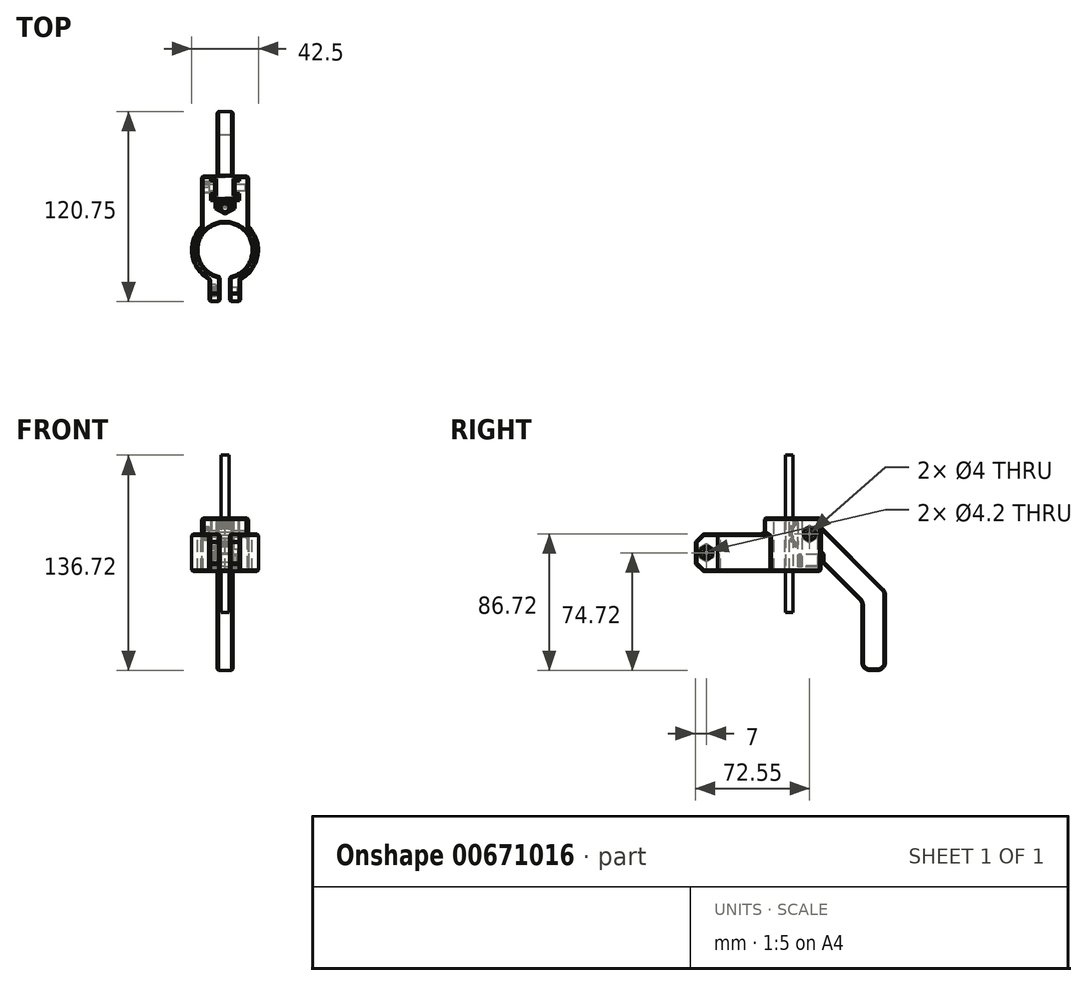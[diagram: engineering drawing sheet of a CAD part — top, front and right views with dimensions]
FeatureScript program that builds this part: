
annotation { "Feature Type Name" : "Feature", "Feature Type Description" : "" }
export const myFeature = defineFeature(function(context is Context, id is Id, definition is map)
    precondition{}
    {
        {
            var Q0;
            Q0=qCreatedBy(makeId("Top.planeOp"),FACE);
            var sketch = newSketch(context, id + "F0", { "sketchPlane" : qUnion([Q0])});
            skArc(sketch, "E0", {"start": v(3, -16.99) * mm, "mid": v(0, 17.25) * mm, "end": v(-3, -16.99) * mm});
            skLineSegment(sketch, "E1.top", {"start": v(3, -32.75) * mm, "end": v(10, -32.75) * mm});
            skLineSegment(sketch, "E1.left", {"start": v(3, -16.99) * mm, "end": v(3, -32.75) * mm});
            skLineSegment(sketch, "E1.right", {"start": v(10, -18.75) * mm, "end": v(10, -32.75) * mm});
            skLineSegment(sketch, "E2.MirrorCS", {"start": v(-10, -18.75) * mm, "end": v(-10, -32.75) * mm});
            skLineSegment(sketch, "E3.MirrorCS", {"start": v(-3, -32.75) * mm, "end": v(-10, -32.75) * mm});
            skLineSegment(sketch, "E4.MirrorCS", {"start": v(-3, -16.99) * mm, "end": v(-3, -32.75) * mm});
            skArc(sketch, "E5.trimOffspring", {"start": v(10, -18.75) * mm, "mid": v(21.02, -3.1) * mm, "end": v(15, 15.05) * mm});
            skArc(sketch, "E6.trimOffspring", {"start": v(-15, 15.05) * mm, "mid": v(-21.02, -3.1) * mm, "end": v(-10, -18.75) * mm});
            skLineSegment(sketch, "E7.top", {"start": v(-15, 47) * mm, "end": v(-5.25, 47) * mm});
            skLineSegment(sketch, "E7.left", {"start": v(-15, 8.52) * mm, "end": v(-15, 47) * mm});
            skLineSegment(sketch, "E7.right", {"start": v(15, 8.52) * mm, "end": v(15, 47) * mm});
            skLineSegment(sketch, "E8", {"start": v(0, 24) * mm, "end": v(-5.25, 27.03) * mm});
            skLineSegment(sketch, "E9", {"start": v(-5.25, 27.03) * mm, "end": v(-5.25, 47) * mm});
            skLineSegment(sketch, "E10", {"start": v(5.25, 47) * mm, "end": v(5.25, 27.03) * mm});
            skLineSegment(sketch, "E11", {"start": v(5.25, 27.03) * mm, "end": v(0, 24) * mm});
            skLineSegment(sketch, "E12.trimOffspring", {"start": v(5.25, 47) * mm, "end": v(15, 47) * mm});
            skSolve(sketch);
        }
        {
            var Q0;
            Q0=qSketchRegion(id+"F0",true);
            extrude(context, id + "F1", {"entities" : qUnion([Q0]), "oppositeDirection" : true, "depth" : 24 * mm, "offsetDistance" : 25 * mm});
        }
        {
            var Q0;
            Q0=makeQuery(id+"F1.opExtrude","SWEPT_FACE",FACE,{"disambiguationData":[OSD([sQuery(id+"F0.wireOp",EDGE,"E2.MirrorCS")])]});
            var sketch = newSketch(context, id + "F2", { "sketchPlane" : qUnion([Q0])});
            skLineSegment(sketch, "E13", {"start": v(25.75, 0) * mm, "end": v(25.75, -24) * mm, "construction": true});
            skCircle(sketch, "E14", {"center": v(25.75, -12) * mm, "radius": 2.1 * mm});
            skCircle(sketch, "E15.cCircle", {"center": v(25.75, -12) * mm, "radius": 3.7 * mm, "construction": true});
            skLineSegment(sketch, "E15.0", {"start": v(25.75, -7.73) * mm, "end": v(29.45, -9.86) * mm});
            skLineSegment(sketch, "E15.1", {"start": v(29.45, -9.86) * mm, "end": v(29.45, -11.5) * mm});
            skLineSegment(sketch, "E15.2", {"start": v(29.45, -14.14) * mm, "end": v(25.75, -16.27) * mm});
            skLineSegment(sketch, "E15.4", {"start": v(22.05, -14.14) * mm, "end": v(22.05, -9.86) * mm});
            skPoint(sketch, "E15.0.midPoint", {"position": v(27.6, -8.8) * mm});
            skLineSegment(sketch, "E16", {"start": v(29.45, -12.5) * mm, "end": v(28.95, -12) * mm});
            skLineSegment(sketch, "E17", {"start": v(28.95, -12) * mm, "end": v(29.45, -11.5) * mm});
            skLineSegment(sketch, "E18.trimOffspring", {"start": v(29.45, -12.5) * mm, "end": v(29.45, -14.14) * mm});
            skLineSegment(sketch, "E19.1.0", {"start": v(24.33, -8.55) * mm, "end": v(25.75, -7.73) * mm});
            skLineSegment(sketch, "E19.1.1", {"start": v(24.33, -8.55) * mm, "end": v(24.15, -9.23) * mm});
            skLineSegment(sketch, "E19.1.2", {"start": v(24.15, -9.23) * mm, "end": v(23.47, -9.05) * mm});
            skLineSegment(sketch, "E19.1.3", {"start": v(22.05, -9.86) * mm, "end": v(23.47, -9.05) * mm});
            skLineSegment(sketch, "E19.2.0", {"start": v(23.47, -14.95) * mm, "end": v(22.05, -14.14) * mm});
            skLineSegment(sketch, "E19.2.1", {"start": v(23.47, -14.95) * mm, "end": v(24.15, -14.77) * mm});
            skLineSegment(sketch, "E19.2.2", {"start": v(24.15, -14.77) * mm, "end": v(24.33, -15.45) * mm});
            skLineSegment(sketch, "E19.2.3", {"start": v(25.75, -16.27) * mm, "end": v(24.33, -15.45) * mm});
            skSolve(sketch);
        }
        {
            var Q0;
            Q0=makeQuery(id+"F2.imprint","IMPRINT",FACE,{"disambiguationData":[TD([[makeQuery(id+"F2.imprint","IMPRINT",EDGE,{"derivedFrom":sQuery(id+"F2.wireOp",EDGE,"E14")}),1.0]])]});
            extrude(context, id + "F3", {"entities" : qUnion([Q0]), "operationType" : NewBodyOperationType.REMOVE, "endBound" : BoundingType.THROUGH_ALL, "oppositeDirection" : true, "depth" : 25 * mm, "offsetDistance" : 25 * mm});
        }
        {
            var Q0;
            Q0=makeQuery(id+"F2.imprint","IMPRINT",FACE,{"disambiguationData":[TD([[makeQuery(id+"F2.imprint","IMPRINT",EDGE,{"derivedFrom":sQuery(id+"F2.wireOp",EDGE,"E14")}),-1.0]])]});
            extrude(context, id + "F4", {"entities" : qUnion([Q0]), "operationType" : NewBodyOperationType.REMOVE, "oppositeDirection" : true, "depth" : 4 * mm, "offsetDistance" : 25 * mm});
        }
        {
            var Q0;
            Q0=qCreatedBy(makeId("Top.planeOp"),FACE);
            var sketch = newSketch(context, id + "F5", { "sketchPlane" : qUnion([Q0])});
            skCircle(sketch, "E20", {"center": v(0, 26.89) * mm, "radius": 2.5 * mm});
            skSolve(sketch);
        }
        {
            var Q0;
            Q0 = qSketchRegion(id + "F5", true);
            extrude(context, id + "F6", {"entities" : qUnion([Q0]), "operationType" : NewBodyOperationType.ADD, "endBound" : BoundingType.SYMMETRIC, "depth" : 100 * mm, "offsetDistance" : 25 * mm});
        }
        {
            var Q0;
            {var subQ5=sQuery(id+"F0.wireOp",EDGE,"E8");Q0=makeQuery(id+"F0.imprint","IMPRINT",FACE,{"disambiguationData":[TD([[makeQuery(id+"F0.imprint","IMPRINT",EDGE,{"derivedFrom":subQ5}),1.0]])]});}
            extrude(context, id + "F7", {"entities" : qUnion([Q0]), "operationType" : NewBodyOperationType.ADD, "depth" : 10 * mm, "offsetDistance" : 25 * mm});
        }
        {
            var Q0;
            Q0=qCreatedBy(makeId("Right.planeOp"),FACE);
            var sketch = newSketch(context, id + "F8", { "sketchPlane" : qUnion([Q0])});
            skCircle(sketch, "E21", {"center": v(37.3, 0) * mm, "radius": 10.5 * mm, "construction": true});
            skLineSegment(sketch, "E22", {"start": v(24.39, -50) * mm, "end": v(24.39, 50) * mm, "construction": true});
            skLineSegment(sketch, "E23", {"start": v(29.39, 50) * mm, "end": v(29.39, -50) * mm, "construction": true});
            skLineSegment(sketch, "E24.bottom", {"start": v(26.8, 1) * mm, "end": v(27.8, 1) * mm});
            skLineSegment(sketch, "E24.top", {"start": v(26.8, -1) * mm, "end": v(27.8, -1) * mm});
            skLineSegment(sketch, "E24.left", {"start": v(26.8, 1) * mm, "end": v(26.8, -1) * mm});
            skLineSegment(sketch, "E25", {"start": v(37.3, 0) * mm, "end": v(26.8, 0) * mm, "construction": true});
            skLineSegment(sketch, "E26", {"start": v(27.8, 1) * mm, "end": v(28.22, 2.95) * mm});
            skLineSegment(sketch, "E27", {"start": v(28, 1.98) * mm, "end": v(37.3, 0) * mm, "construction": true});
            skLineSegment(sketch, "E28.1.0", {"start": v(28.11, -5.18) * mm, "end": v(29.03, -4.78) * mm});
            skLineSegment(sketch, "E28.1.1", {"start": v(27.3, -3.36) * mm, "end": v(28.22, -2.95) * mm});
            skLineSegment(sketch, "E28.1.2", {"start": v(27.3, -3.36) * mm, "end": v(28.11, -5.18) * mm});
            skLineSegment(sketch, "E28.1.3", {"start": v(28.22, -2.95) * mm, "end": v(27.8, -1) * mm});
            skLineSegment(sketch, "E28.2.0", {"start": v(31.02, -8.47) * mm, "end": v(31.69, -7.73) * mm});
            skLineSegment(sketch, "E28.2.1", {"start": v(29.53, -7.13) * mm, "end": v(30.2, -6.4) * mm});
            skLineSegment(sketch, "E28.2.2", {"start": v(29.53, -7.13) * mm, "end": v(31.02, -8.47) * mm});
            skLineSegment(sketch, "E28.2.3", {"start": v(30.2, -6.4) * mm, "end": v(29.03, -4.78) * mm});
            skLineSegment(sketch, "E28.3.0", {"start": v(35, -10.3) * mm, "end": v(35.31, -9.34) * mm});
            skLineSegment(sketch, "E28.3.1", {"start": v(33.1, -9.68) * mm, "end": v(33.41, -8.73) * mm});
            skLineSegment(sketch, "E28.3.2", {"start": v(33.1, -9.68) * mm, "end": v(35, -10.3) * mm});
            skLineSegment(sketch, "E28.3.3", {"start": v(33.41, -8.73) * mm, "end": v(31.69, -7.73) * mm});
            skLineSegment(sketch, "E28.4.0", {"start": v(39.4, -10.34) * mm, "end": v(39.29, -9.34) * mm});
            skLineSegment(sketch, "E28.4.1", {"start": v(37.4, -10.55) * mm, "end": v(37.3, -9.55) * mm});
            skLineSegment(sketch, "E28.4.2", {"start": v(37.4, -10.55) * mm, "end": v(39.4, -10.34) * mm});
            skLineSegment(sketch, "E28.4.3", {"start": v(37.3, -9.55) * mm, "end": v(35.31, -9.34) * mm});
            skLineSegment(sketch, "E28.5.1", {"start": v(41.69, -9.6) * mm, "end": v(41.19, -8.73) * mm});
            skLineSegment(sketch, "E28.5.2", {"start": v(41.69, -9.6) * mm, "end": v(43.41, -8.6) * mm});
            skLineSegment(sketch, "E28.5.3", {"start": v(41.19, -8.73) * mm, "end": v(39.29, -9.34) * mm});
            skLineSegment(sketch, "E28.10.0", {"start": v(41.69, 9.6) * mm, "end": v(41.19, 8.73) * mm});
            skLineSegment(sketch, "E28.11.0", {"start": v(37.4, 10.55) * mm, "end": v(37.3, 9.55) * mm});
            skLineSegment(sketch, "E28.11.1", {"start": v(39.4, 10.34) * mm, "end": v(39.29, 9.34) * mm});
            skLineSegment(sketch, "E28.11.2", {"start": v(39.4, 10.34) * mm, "end": v(37.4, 10.55) * mm});
            skLineSegment(sketch, "E28.11.3", {"start": v(39.29, 9.34) * mm, "end": v(41.19, 8.73) * mm});
            skCircle(sketch, "E29", {"center": v(39.8, 0) * mm, "radius": 2 * mm});
            skLineSegment(sketch, "E30.1.12.0", {"start": v(33.1, 9.68) * mm, "end": v(33.41, 8.73) * mm});
            skLineSegment(sketch, "E30.3.12.0", {"start": v(35, 10.3) * mm, "end": v(35.31, 9.34) * mm});
            skLineSegment(sketch, "E30.6.12.0", {"start": v(35, 10.3) * mm, "end": v(33.1, 9.68) * mm});
            skLineSegment(sketch, "E30.9.12.0", {"start": v(35.31, 9.34) * mm, "end": v(37.3, 9.55) * mm});
            skLineSegment(sketch, "E30.1.13.0", {"start": v(29.53, 7.13) * mm, "end": v(30.2, 6.4) * mm});
            skLineSegment(sketch, "E30.3.13.0", {"start": v(31.02, 8.47) * mm, "end": v(31.69, 7.73) * mm});
            skLineSegment(sketch, "E30.6.13.0", {"start": v(31.02, 8.47) * mm, "end": v(29.53, 7.13) * mm});
            skLineSegment(sketch, "E30.9.13.0", {"start": v(31.69, 7.73) * mm, "end": v(33.41, 8.73) * mm});
            skLineSegment(sketch, "E30.1.14.0", {"start": v(27.3, 3.36) * mm, "end": v(28.22, 2.95) * mm});
            skLineSegment(sketch, "E30.3.14.0", {"start": v(28.11, 5.18) * mm, "end": v(29.03, 4.78) * mm});
            skLineSegment(sketch, "E30.6.14.0", {"start": v(28.11, 5.18) * mm, "end": v(27.3, 3.36) * mm});
            skLineSegment(sketch, "E30.9.14.0", {"start": v(29.03, 4.78) * mm, "end": v(30.2, 6.4) * mm});
            skLineSegment(sketch, "E31", {"start": v(43.41, -8.6) * mm, "end": v(48, -13.18) * mm});
            skLineSegment(sketch, "E32", {"start": v(48, -13.18) * mm, "end": v(48, -18.18) * mm});
            skLineSegment(sketch, "E33", {"start": v(88, -36.72) * mm, "end": v(41.69, 9.6) * mm});
            skLineSegment(sketch, "E34", {"start": v(48, -18.18) * mm, "end": v(73, -43.18) * mm});
            skLineSegment(sketch, "E35", {"start": v(73, -43.18) * mm, "end": v(73, -86.72) * mm});
            skLineSegment(sketch, "E36", {"start": v(73, -86.72) * mm, "end": v(88, -86.72) * mm});
            skLineSegment(sketch, "E37", {"start": v(88, -86.72) * mm, "end": v(88, -36.72) * mm});
            skSolve(sketch);
        }
        {
            var Q0;
            Q0=makeQuery(id+"F8.imprint","IMPRINT",FACE,{"disambiguationData":[TD([[makeQuery(id+"F8.imprint","IMPRINT",EDGE,{"derivedFrom":sQuery(id+"F8.wireOp",EDGE,"E29")}),1.0]])]});
            extrude(context, id + "F9", {"entities" : qUnion([Q0]), "operationType" : NewBodyOperationType.REMOVE, "endBound" : BoundingType.SYMMETRIC, "oppositeDirection" : true, "depth" : 100 * mm, "offsetDistance" : 25 * mm});
        }
        {
            var Q0;
            Q0 = qSketchRegion(id + "F8", true);
            extrude(context, id + "F10", {"entities" : qUnion([Q0]), "endBound" : BoundingType.SYMMETRIC, "depth" : 10 * mm, "offsetDistance" : 25 * mm});
        }
        {
            var Q0;
            Q0=makeQuery(id+"F10.opExtrude","SWEPT_EDGE",EDGE,{"disambiguationData":[OSD([sQuery(id+"F8.wireOp",EDGE,"E34"),sQuery(id+"F8.wireOp",EDGE,"E35")])]});
            var Q1;
            Q1=makeQuery(id+"F10.opExtrude","SWEPT_EDGE",EDGE,{"disambiguationData":[OSD([sQuery(id+"F8.wireOp",EDGE,"E35"),sQuery(id+"F8.wireOp",EDGE,"E36")])]});
            var Q2;
            Q2=makeQuery(id+"F10.opExtrude","SWEPT_EDGE",EDGE,{"disambiguationData":[OSD([sQuery(id+"F8.wireOp",EDGE,"E36"),sQuery(id+"F8.wireOp",EDGE,"E37")])]});
            var Q3;
            Q3=makeQuery(id+"F10.opExtrude","SWEPT_EDGE",EDGE,{"disambiguationData":[OSD([sQuery(id+"F8.wireOp",EDGE,"E33"),sQuery(id+"F8.wireOp",EDGE,"E37")])]});
            var Q4;
            Q4=makeQuery(id+"F10.opExtrude","SWEPT_EDGE",EDGE,{"disambiguationData":[OSD([sQuery(id+"F8.wireOp",EDGE,"E28.10.0"),sQuery(id+"F8.wireOp",EDGE,"E33")])]});
            var Q5;
            Q5=makeQuery(id+"F10.opExtrude","SWEPT_EDGE",EDGE,{"disambiguationData":[OSD([sQuery(id+"F8.wireOp",EDGE,"E28.5.2"),sQuery(id+"F8.wireOp",EDGE,"E31")])]});
            fillet(context, id + "F11", {"entities" : qUnion([Q0, Q1, Q2, Q3, Q4, Q5]), "radius" : 5 * mm, "tangentPropagation" : true, "allowEdgeOverflow" : false});
        }
        {
            var Q0;
            Q0=makeQuery(id+"F10.opExtrude","CAP_FACE",FACE,{"disambiguationData":[OSD([sQuery(id+"F8.wireOp",EDGE,"E24.bottom"),sQuery(id+"F8.wireOp",EDGE,"E24.top"),sQuery(id+"F8.wireOp",EDGE,"E24.left"),sQuery(id+"F8.wireOp",EDGE,"E26"),sQuery(id+"F8.wireOp",EDGE,"E28.1.0"),sQuery(id+"F8.wireOp",EDGE,"E28.1.1"),sQuery(id+"F8.wireOp",EDGE,"E28.1.2"),sQuery(id+"F8.wireOp",EDGE,"E28.1.3"),sQuery(id+"F8.wireOp",EDGE,"E28.2.0"),sQuery(id+"F8.wireOp",EDGE,"E28.2.1"),sQuery(id+"F8.wireOp",EDGE,"E28.2.2"),sQuery(id+"F8.wireOp",EDGE,"E28.2.3"),sQuery(id+"F8.wireOp",EDGE,"E28.3.0"),sQuery(id+"F8.wireOp",EDGE,"E28.3.1"),sQuery(id+"F8.wireOp",EDGE,"E28.3.2"),sQuery(id+"F8.wireOp",EDGE,"E28.3.3"),sQuery(id+"F8.wireOp",EDGE,"E28.4.0"),sQuery(id+"F8.wireOp",EDGE,"E28.4.1"),sQuery(id+"F8.wireOp",EDGE,"E28.4.2"),sQuery(id+"F8.wireOp",EDGE,"E28.4.3"),sQuery(id+"F8.wireOp",EDGE,"E28.5.1"),sQuery(id+"F8.wireOp",EDGE,"E28.5.2"),sQuery(id+"F8.wireOp",EDGE,"E28.5.3"),sQuery(id+"F8.wireOp",EDGE,"E28.10.0"),sQuery(id+"F8.wireOp",EDGE,"E28.11.0"),sQuery(id+"F8.wireOp",EDGE,"E28.11.1"),sQuery(id+"F8.wireOp",EDGE,"E28.11.2"),sQuery(id+"F8.wireOp",EDGE,"E28.11.3"),sQuery(id+"F8.wireOp",EDGE,"E29"),sQuery(id+"F8.wireOp",EDGE,"E30.1.12.0"),sQuery(id+"F8.wireOp",EDGE,"E30.3.12.0"),sQuery(id+"F8.wireOp",EDGE,"E30.6.12.0"),sQuery(id+"F8.wireOp",EDGE,"E30.9.12.0"),sQuery(id+"F8.wireOp",EDGE,"E30.1.13.0"),sQuery(id+"F8.wireOp",EDGE,"E30.3.13.0"),sQuery(id+"F8.wireOp",EDGE,"E30.6.13.0"),sQuery(id+"F8.wireOp",EDGE,"E30.9.13.0"),sQuery(id+"F8.wireOp",EDGE,"E30.1.14.0"),sQuery(id+"F8.wireOp",EDGE,"E30.3.14.0"),sQuery(id+"F8.wireOp",EDGE,"E30.6.14.0"),sQuery(id+"F8.wireOp",EDGE,"E30.9.14.0"),sQuery(id+"F8.wireOp",EDGE,"E31"),sQuery(id+"F8.wireOp",EDGE,"E32"),sQuery(id+"F8.wireOp",EDGE,"E33"),sQuery(id+"F8.wireOp",EDGE,"E34"),sQuery(id+"F8.wireOp",EDGE,"E35"),sQuery(id+"F8.wireOp",EDGE,"E36"),sQuery(id+"F8.wireOp",EDGE,"E37")])],"isStart":false});
            var Q1;
            Q1=makeQuery(id+"F10.opExtrude","CAP_FACE",FACE,{"disambiguationData":[OSD([sQuery(id+"F8.wireOp",EDGE,"E24.bottom"),sQuery(id+"F8.wireOp",EDGE,"E24.top"),sQuery(id+"F8.wireOp",EDGE,"E24.left"),sQuery(id+"F8.wireOp",EDGE,"E26"),sQuery(id+"F8.wireOp",EDGE,"E28.1.0"),sQuery(id+"F8.wireOp",EDGE,"E28.1.1"),sQuery(id+"F8.wireOp",EDGE,"E28.1.2"),sQuery(id+"F8.wireOp",EDGE,"E28.1.3"),sQuery(id+"F8.wireOp",EDGE,"E28.2.0"),sQuery(id+"F8.wireOp",EDGE,"E28.2.1"),sQuery(id+"F8.wireOp",EDGE,"E28.2.2"),sQuery(id+"F8.wireOp",EDGE,"E28.2.3"),sQuery(id+"F8.wireOp",EDGE,"E28.3.0"),sQuery(id+"F8.wireOp",EDGE,"E28.3.1"),sQuery(id+"F8.wireOp",EDGE,"E28.3.2"),sQuery(id+"F8.wireOp",EDGE,"E28.3.3"),sQuery(id+"F8.wireOp",EDGE,"E28.4.0"),sQuery(id+"F8.wireOp",EDGE,"E28.4.1"),sQuery(id+"F8.wireOp",EDGE,"E28.4.2"),sQuery(id+"F8.wireOp",EDGE,"E28.4.3"),sQuery(id+"F8.wireOp",EDGE,"E28.5.1"),sQuery(id+"F8.wireOp",EDGE,"E28.5.2"),sQuery(id+"F8.wireOp",EDGE,"E28.5.3"),sQuery(id+"F8.wireOp",EDGE,"E28.10.0"),sQuery(id+"F8.wireOp",EDGE,"E28.11.0"),sQuery(id+"F8.wireOp",EDGE,"E28.11.1"),sQuery(id+"F8.wireOp",EDGE,"E28.11.2"),sQuery(id+"F8.wireOp",EDGE,"E28.11.3"),sQuery(id+"F8.wireOp",EDGE,"E29"),sQuery(id+"F8.wireOp",EDGE,"E30.1.12.0"),sQuery(id+"F8.wireOp",EDGE,"E30.3.12.0"),sQuery(id+"F8.wireOp",EDGE,"E30.6.12.0"),sQuery(id+"F8.wireOp",EDGE,"E30.9.12.0"),sQuery(id+"F8.wireOp",EDGE,"E30.1.13.0"),sQuery(id+"F8.wireOp",EDGE,"E30.3.13.0"),sQuery(id+"F8.wireOp",EDGE,"E30.6.13.0"),sQuery(id+"F8.wireOp",EDGE,"E30.9.13.0"),sQuery(id+"F8.wireOp",EDGE,"E30.1.14.0"),sQuery(id+"F8.wireOp",EDGE,"E30.3.14.0"),sQuery(id+"F8.wireOp",EDGE,"E30.6.14.0"),sQuery(id+"F8.wireOp",EDGE,"E30.9.14.0"),sQuery(id+"F8.wireOp",EDGE,"E31"),sQuery(id+"F8.wireOp",EDGE,"E32"),sQuery(id+"F8.wireOp",EDGE,"E33"),sQuery(id+"F8.wireOp",EDGE,"E34"),sQuery(id+"F8.wireOp",EDGE,"E35"),sQuery(id+"F8.wireOp",EDGE,"E36"),sQuery(id+"F8.wireOp",EDGE,"E37")])],"isStart":true});
            chamfer(context, id + "F12", {"entities" : qUnion([Q0, Q1]), "width" : 0.9 * mm, "tangentPropagation" : true});
        }
        {
            var Q0;
            Q0=makeQuery(id+"F1.opExtrude","CAP_FACE",FACE,{"disambiguationData":[OSD([sQuery(id+"F0.wireOp",EDGE,"E0"),sQuery(id+"F0.wireOp",EDGE,"E1.top"),sQuery(id+"F0.wireOp",EDGE,"E1.left"),sQuery(id+"F0.wireOp",EDGE,"E1.right"),sQuery(id+"F0.wireOp",EDGE,"E2.MirrorCS"),sQuery(id+"F0.wireOp",EDGE,"E3.MirrorCS"),sQuery(id+"F0.wireOp",EDGE,"E4.MirrorCS"),sQuery(id+"F0.wireOp",EDGE,"E5.trimOffspring"),sQuery(id+"F0.wireOp",EDGE,"E6.trimOffspring"),sQuery(id+"F0.wireOp",EDGE,"E7.top"),sQuery(id+"F0.wireOp",EDGE,"E7.left"),sQuery(id+"F0.wireOp",EDGE,"E7.right"),sQuery(id+"F0.wireOp",EDGE,"E8"),sQuery(id+"F0.wireOp",EDGE,"E9"),sQuery(id+"F0.wireOp",EDGE,"E10"),sQuery(id+"F0.wireOp",EDGE,"E11"),sQuery(id+"F0.wireOp",EDGE,"E12.trimOffspring")])],"isStart":false});
            cPlane(context, id + "F13", {"entities" : qUnion([Q0]), "cplaneType" : CPlaneType.OFFSET, "offset" : 3 * mm, "oppositeDirection" : true, "width" : 150 * mm, "height" : 150 * mm});
        }
        {
            var Q0;
            Q0=qCreatedBy(id+"F13.planeOp",FACE);
            var sketch = newSketch(context, id + "F14", { "sketchPlane" : qUnion([Q0])});
            skLineSegment(sketch, "E38", {"start": v(8, -32.6) * mm, "end": v(-8, -32.6) * mm});
            skLineSegment(sketch, "E39", {"start": v(-8, -34.6) * mm, "end": v(-8, -32.6) * mm});
            skLineSegment(sketch, "E40", {"start": v(-8, -34.6) * mm, "end": v(-5.25, -34.6) * mm});
            skLineSegment(sketch, "E41", {"start": v(-5.25, -45) * mm, "end": v(-5.25, -34.6) * mm});
            skLineSegment(sketch, "E42", {"start": v(-5.25, -45) * mm, "end": v(-8, -45) * mm});
            skLineSegment(sketch, "E43", {"start": v(-8, -47) * mm, "end": v(-8, -45) * mm});
            skLineSegment(sketch, "E44", {"start": v(-8, -47) * mm, "end": v(8, -47) * mm});
            skLineSegment(sketch, "E45.MirrorCS", {"start": v(8, -34.6) * mm, "end": v(5.25, -34.6) * mm});
            skLineSegment(sketch, "E46.MirrorCS", {"start": v(5.25, -45) * mm, "end": v(8, -45) * mm});
            skLineSegment(sketch, "E47.MirrorCS", {"start": v(8, -45) * mm, "end": v(8, -47) * mm});
            skLineSegment(sketch, "E48.MirrorCS", {"start": v(8, -34.6) * mm, "end": v(8, -32.6) * mm});
            skLineSegment(sketch, "E49.MirrorCS", {"start": v(5.25, -45) * mm, "end": v(5.25, -34.6) * mm});
            skLineSegment(sketch, "E50", {"start": v(-5.25, -39.8) * mm, "end": v(5.25, -39.8) * mm, "construction": true});
            skLineSegment(sketch, "E51.0", {"start": v(8.2, -34.8) * mm, "end": v(8.2, -32.4) * mm});
            skLineSegment(sketch, "E51.1", {"start": v(-5.45, -44.8) * mm, "end": v(-8.2, -44.8) * mm});
            skLineSegment(sketch, "E51.2", {"start": v(-5.45, -44.8) * mm, "end": v(-5.45, -34.8) * mm});
            skLineSegment(sketch, "E51.3", {"start": v(-8.2, -34.8) * mm, "end": v(-5.45, -34.8) * mm});
            skLineSegment(sketch, "E51.4", {"start": v(-8.2, -34.8) * mm, "end": v(-8.2, -32.4) * mm});
            skLineSegment(sketch, "E51.5", {"start": v(-8.2, -47.2) * mm, "end": v(-8.2, -44.8) * mm});
            skLineSegment(sketch, "E51.6", {"start": v(8.2, -32.4) * mm, "end": v(-8.2, -32.4) * mm});
            skLineSegment(sketch, "E51.7", {"start": v(-8.2, -47.2) * mm, "end": v(8.2, -47.2) * mm});
            skLineSegment(sketch, "E51.8", {"start": v(8.2, -44.8) * mm, "end": v(8.2, -47.2) * mm});
            skLineSegment(sketch, "E51.9", {"start": v(5.45, -44.8) * mm, "end": v(8.2, -44.8) * mm});
            skLineSegment(sketch, "E51.10", {"start": v(5.45, -44.8) * mm, "end": v(5.45, -34.8) * mm});
            skLineSegment(sketch, "E51.11", {"start": v(8.2, -34.8) * mm, "end": v(5.45, -34.8) * mm});
            skSolve(sketch);
        }
        {
            var Q0;
            Q0 = qSketchRegion(id + "F14", true);
            var Q1;
            Q1=makeQuery(id+"F14.imprint","IMPRINT",FACE,{"disambiguationData":[TD([[makeQuery(id+"F14.imprint","IMPRINT",EDGE,{"derivedFrom":sQuery(id+"F14.wireOp",EDGE,"E38")}),1.0]])]});
            extrude(context, id + "F15", {"entities" : qUnion([Q0, Q1]), "operationType" : NewBodyOperationType.REMOVE, "endBound" : BoundingType.THROUGH_ALL, "oppositeDirection" : true, "depth" : 25 * mm, "offsetDistance" : 25 * mm});
        }
        {
            var Q0;
            Q0=makeQuery(id+"F14.imprint","IMPRINT",FACE,{"disambiguationData":[TD([[makeQuery(id+"F14.imprint","IMPRINT",EDGE,{"derivedFrom":sQuery(id+"F14.wireOp",EDGE,"E38")}),1.0]])]});
            var Q1;
            Q1=sQuery(id+"F8.wireOp",VERTEX,"E32.start");
            extrude(context, id + "F16", {"entities" : qUnion([Q0]), "endBound" : BoundingType.UP_TO_VERTEX, "oppositeDirection" : true, "depth" : 25 * mm, "endBoundEntityVertex" : qUnion([Q1]), "offsetDistance" : 25 * mm});
        }
        {
            var Q0;
            Q0=makeQuery(id+"F16.opExtrude","CAP_FACE",FACE,{"disambiguationData":[OSD([sQuery(id+"F14.wireOp",EDGE,"E38"),sQuery(id+"F14.wireOp",EDGE,"E39"),sQuery(id+"F14.wireOp",EDGE,"E40"),sQuery(id+"F14.wireOp",EDGE,"E41"),sQuery(id+"F14.wireOp",EDGE,"E42"),sQuery(id+"F14.wireOp",EDGE,"E43"),sQuery(id+"F14.wireOp",EDGE,"E44"),sQuery(id+"F14.wireOp",EDGE,"E45.MirrorCS"),sQuery(id+"F14.wireOp",EDGE,"E46.MirrorCS"),sQuery(id+"F14.wireOp",EDGE,"E47.MirrorCS"),sQuery(id+"F14.wireOp",EDGE,"E48.MirrorCS"),sQuery(id+"F14.wireOp",EDGE,"E49.MirrorCS")])],"isStart":true});
            var Q1;
            Q1=makeQuery(id+"F16.opExtrude","CAP_FACE",FACE,{"disambiguationData":[OSD([dummyQuery(id+"F16.vertexPlane.planeOp",FACE)])],"isStart":false});
            var Q2;
            Q2=makeQuery(id+"F16.opExtrude","SWEPT_FACE",FACE,{"disambiguationData":[OSD([sQuery(id+"F14.wireOp",EDGE,"E48.MirrorCS")])]});
            var Q3;
            Q3=makeQuery(id+"F16.opExtrude","SWEPT_FACE",FACE,{"disambiguationData":[OSD([sQuery(id+"F14.wireOp",EDGE,"E47.MirrorCS")])]});
            var Q4;
            Q4=makeQuery(id+"F16.opExtrude","SWEPT_FACE",FACE,{"disambiguationData":[OSD([sQuery(id+"F14.wireOp",EDGE,"E43")])]});
            var Q5;
            Q5=makeQuery(id+"F16.opExtrude","SWEPT_FACE",FACE,{"disambiguationData":[OSD([sQuery(id+"F14.wireOp",EDGE,"E39")])]});
            chamfer(context, id + "F17", {"entities" : qUnion([Q0, Q1, Q2, Q3, Q4, Q5]), "width" : 0.6 * mm, "tangentPropagation" : true});
        }
        {
            var Q0;
            {var subQ0=sQuery(id+"F0.wireOp",EDGE,"E7.left");Q0=makeQuery(id+"F7.boolean.opBoolean","MERGE",FACE,{"derivedFrom":[makeQuery(id+"F1.opExtrude","SWEPT_FACE",FACE,{"disambiguationData":[OSD([subQ0])]}),makeQuery(id+"F7.opExtrude","SWEPT_FACE",FACE,{"disambiguationData":[OSD([subQ0])]})]});}
            var sketch = newSketch(context, id + "F18", { "sketchPlane" : qUnion([Q0])});
            skCircle(sketch, "E52.cCircle", {"center": v(-39.8, 0) * mm, "radius": 3.7 * mm, "construction": true});
            skLineSegment(sketch, "E52.0", {"start": v(-39.8, 4.27) * mm, "end": v(-36.1, 2.14) * mm});
            skLineSegment(sketch, "E52.1", {"start": v(-36.1, 2.14) * mm, "end": v(-36.1, 0.5) * mm});
            skLineSegment(sketch, "E52.2", {"start": v(-36.1, -2.14) * mm, "end": v(-39.8, -4.27) * mm});
            skLineSegment(sketch, "E52.4", {"start": v(-43.5, -2.14) * mm, "end": v(-43.5, 2.14) * mm});
            skPoint(sketch, "E52.0.midPoint", {"position": v(-37.95, 3.2) * mm});
            skLineSegment(sketch, "E53", {"start": v(-36.1, -0.5) * mm, "end": v(-36.6, 0) * mm});
            skLineSegment(sketch, "E54", {"start": v(-36.6, 0) * mm, "end": v(-36.1, 0.5) * mm});
            skLineSegment(sketch, "E55.trimOffspring", {"start": v(-36.1, -0.5) * mm, "end": v(-36.1, -2.14) * mm});
            skLineSegment(sketch, "E56.1.0", {"start": v(-41.22, 3.45) * mm, "end": v(-39.8, 4.27) * mm});
            skLineSegment(sketch, "E56.1.1", {"start": v(-41.22, 3.45) * mm, "end": v(-41.4, 2.77) * mm});
            skLineSegment(sketch, "E56.1.2", {"start": v(-41.4, 2.77) * mm, "end": v(-42.08, 2.95) * mm});
            skLineSegment(sketch, "E56.1.3", {"start": v(-43.5, 2.14) * mm, "end": v(-42.08, 2.95) * mm});
            skLineSegment(sketch, "E56.2.0", {"start": v(-42.08, -2.95) * mm, "end": v(-43.5, -2.14) * mm});
            skLineSegment(sketch, "E56.2.1", {"start": v(-42.08, -2.95) * mm, "end": v(-41.4, -2.77) * mm});
            skLineSegment(sketch, "E56.2.2", {"start": v(-41.4, -2.77) * mm, "end": v(-41.22, -3.45) * mm});
            skLineSegment(sketch, "E56.2.3", {"start": v(-39.8, -4.27) * mm, "end": v(-41.22, -3.45) * mm});
            skSolve(sketch);
        }
        {
            var Q0;
            Q0 = qSketchRegion(id + "F18", true);
            extrude(context, id + "F19", {"entities" : qUnion([Q0]), "operationType" : NewBodyOperationType.REMOVE, "oppositeDirection" : true, "depth" : 5 * mm, "offsetDistance" : 25 * mm});
        }
        {
            var Q0;
            Q0=makeQuery(id+"F3.boolean.opBoolean","INTERSECT",EDGE,{"derivedFrom":[makeQuery(id+"F1.opExtrude","SWEPT_FACE",FACE,{"disambiguationData":[OSD([sQuery(id+"F0.wireOp",EDGE,"E1.right")])]}),makeQuery(id+"F3.opExtrude","SWEPT_FACE",FACE,{"disambiguationData":[OSD([sQuery(id+"F2.wireOp",EDGE,"E14")])]})]});
            var Q1;
            {var subQ0=sQuery(id+"F0.wireOp",EDGE,"E7.right");Q1=makeQuery(id+"F9.boolean.opBoolean","INTERSECT",EDGE,{"derivedFrom":[makeQuery(id+"F7.boolean.opBoolean","MERGE",FACE,{"derivedFrom":[makeQuery(id+"F1.opExtrude","SWEPT_FACE",FACE,{"disambiguationData":[OSD([subQ0])]}),makeQuery(id+"F7.opExtrude","SWEPT_FACE",FACE,{"disambiguationData":[OSD([subQ0])]})]}),makeQuery(id+"F9.opExtrude","SWEPT_FACE",FACE,{"disambiguationData":[OSD([sQuery(id+"F8.wireOp",EDGE,"E29")])]})]});}
            var Q2;
            {var subQ0=sQuery(id+"F0.wireOp",EDGE,"E7.right");Q2=makeQuery(id+"FyBhXYofOcvtQ58_5.boolean.opBoolean","INTERSECT",EDGE,{"derivedFrom":[makeQuery(id+"F7.boolean.opBoolean","MERGE",FACE,{"derivedFrom":[makeQuery(id+"F1.opExtrude","SWEPT_FACE",FACE,{"disambiguationData":[OSD([subQ0])]}),makeQuery(id+"F7.opExtrude","SWEPT_FACE",FACE,{"disambiguationData":[OSD([subQ0])]})]}),makeQuery(id+"FyBhXYofOcvtQ58_5.opExtrude","SWEPT_FACE",FACE,{"disambiguationData":[OSD([sQuery(id+"FaaSlcbahXEhdMI_5.wireOp",EDGE,"exEu7dH0-lp8G-LPu1-6jyY-PFkxikVfgg87")])]})]});}
            chamfer(context, id + "F20", {"entities" : qUnion([Q0, Q1, Q2]), "width" : 2 * mm, "tangentPropagation" : true});
        }
        {
            var Q0;
            Q0=makeQuery(id+"F1.opExtrude","CAP_EDGE",EDGE,{"disambiguationData":[OSD([sQuery(id+"F0.wireOp",EDGE,"E3.MirrorCS")])],"isStart":true});
            var Q1;
            Q1=makeQuery(id+"F1.opExtrude","CAP_EDGE",EDGE,{"disambiguationData":[OSD([sQuery(id+"F0.wireOp",EDGE,"E1.top")])],"isStart":true});
            var Q2;
            Q2=makeQuery(id+"F1.opExtrude","CAP_EDGE",EDGE,{"disambiguationData":[OSD([sQuery(id+"F0.wireOp",EDGE,"E1.top")])],"isStart":false});
            var Q3;
            Q3=makeQuery(id+"F1.opExtrude","CAP_EDGE",EDGE,{"disambiguationData":[OSD([sQuery(id+"F0.wireOp",EDGE,"E3.MirrorCS")])],"isStart":false});
            chamfer(context, id + "F21", {"entities" : qUnion([Q0, Q1, Q2, Q3]), "width" : 5 * mm, "tangentPropagation" : true});
        }
        {
            var Q0;
            {var subQ0=sQuery(id+"F0.wireOp",EDGE,"E4.MirrorCS");var subQ1=sQuery(id+"F0.wireOp",EDGE,"E3.MirrorCS");var subQ2=sQuery(id+"F0.wireOp",EDGE,"E2.MirrorCS");var subQ3=sQuery(id+"F0.wireOp",EDGE,"E7.left");var subQ4=sQuery(id+"F0.wireOp",EDGE,"E0");var subQ5=sQuery(id+"F0.wireOp",EDGE,"E6.trimOffspring");Q0=makeQuery(id+"F7.boolean.opBoolean","SPLIT",FACE,{"disambiguationData":[TD([makeQuery(id+"F1.opExtrude","SWEPT_FACE",FACE,{"disambiguationData":[OSD([subQ2])]})])],"derivedFrom":makeQuery(id+"F1.opExtrude","CAP_FACE",FACE,{"disambiguationData":[OSD([subQ4,sQuery(id+"F0.wireOp",EDGE,"E1.top"),sQuery(id+"F0.wireOp",EDGE,"E1.left"),sQuery(id+"F0.wireOp",EDGE,"E1.right"),subQ2,subQ1,subQ0,sQuery(id+"F0.wireOp",EDGE,"E5.trimOffspring"),subQ5,sQuery(id+"F0.wireOp",EDGE,"E7.top"),subQ3,sQuery(id+"F0.wireOp",EDGE,"E7.right"),sQuery(id+"F0.wireOp",EDGE,"E8"),sQuery(id+"F0.wireOp",EDGE,"E9"),sQuery(id+"F0.wireOp",EDGE,"E10"),sQuery(id+"F0.wireOp",EDGE,"E11"),sQuery(id+"F0.wireOp",EDGE,"oxaJkNi3-Ak0Z-1hdz-Ji0s-hlfaC5dMFClf")])],"isStart":true})});}
            var Q1;
            {var subQ0=sQuery(id+"F0.wireOp",EDGE,"E1.left");var subQ1=sQuery(id+"F0.wireOp",EDGE,"E1.top");var subQ2=sQuery(id+"F0.wireOp",EDGE,"E1.right");var subQ3=sQuery(id+"F0.wireOp",EDGE,"E0");var subQ4=sQuery(id+"F0.wireOp",EDGE,"E5.trimOffspring");var subQ5=sQuery(id+"F0.wireOp",EDGE,"E7.right");Q1=makeQuery(id+"F7.boolean.opBoolean","SPLIT",FACE,{"disambiguationData":[TD([makeQuery(id+"F1.opExtrude","SWEPT_FACE",FACE,{"disambiguationData":[OSD([subQ1])]})])],"derivedFrom":makeQuery(id+"F1.opExtrude","CAP_FACE",FACE,{"disambiguationData":[OSD([subQ3,subQ1,subQ0,subQ2,sQuery(id+"F0.wireOp",EDGE,"E2.MirrorCS"),sQuery(id+"F0.wireOp",EDGE,"E3.MirrorCS"),sQuery(id+"F0.wireOp",EDGE,"E4.MirrorCS"),subQ4,sQuery(id+"F0.wireOp",EDGE,"E6.trimOffspring"),sQuery(id+"F0.wireOp",EDGE,"E7.top"),sQuery(id+"F0.wireOp",EDGE,"E7.left"),subQ5,sQuery(id+"F0.wireOp",EDGE,"E8"),sQuery(id+"F0.wireOp",EDGE,"E9"),sQuery(id+"F0.wireOp",EDGE,"E10"),sQuery(id+"F0.wireOp",EDGE,"E11"),sQuery(id+"F0.wireOp",EDGE,"oxaJkNi3-Ak0Z-1hdz-Ji0s-hlfaC5dMFClf")])],"isStart":true})});}
            var Q2;
            Q2=makeQuery(id+"F1.opExtrude","CAP_FACE",FACE,{"disambiguationData":[OSD([sQuery(id+"F0.wireOp",EDGE,"E0"),sQuery(id+"F0.wireOp",EDGE,"E1.top"),sQuery(id+"F0.wireOp",EDGE,"E1.left"),sQuery(id+"F0.wireOp",EDGE,"E1.right"),sQuery(id+"F0.wireOp",EDGE,"E2.MirrorCS"),sQuery(id+"F0.wireOp",EDGE,"E3.MirrorCS"),sQuery(id+"F0.wireOp",EDGE,"E4.MirrorCS"),sQuery(id+"F0.wireOp",EDGE,"E5.trimOffspring"),sQuery(id+"F0.wireOp",EDGE,"E6.trimOffspring"),sQuery(id+"F0.wireOp",EDGE,"E7.top"),sQuery(id+"F0.wireOp",EDGE,"E7.left"),sQuery(id+"F0.wireOp",EDGE,"E7.right"),sQuery(id+"F0.wireOp",EDGE,"E8"),sQuery(id+"F0.wireOp",EDGE,"E9"),sQuery(id+"F0.wireOp",EDGE,"E10"),sQuery(id+"F0.wireOp",EDGE,"E11"),sQuery(id+"F0.wireOp",EDGE,"oxaJkNi3-Ak0Z-1hdz-Ji0s-hlfaC5dMFClf")])],"isStart":false});
            var Q3;
            Q3=makeQuery(id+"F1.opExtrude","SWEPT_FACE",FACE,{"disambiguationData":[OSD([sQuery(id+"F0.wireOp",EDGE,"E1.top")])]});
            var Q4;
            Q4=makeQuery(id+"F1.opExtrude","SWEPT_FACE",FACE,{"disambiguationData":[OSD([sQuery(id+"F0.wireOp",EDGE,"E3.MirrorCS")])]});
            var Q5;
            Q5=makeQuery(id+"F7.opExtrude","CAP_FACE",FACE,{"disambiguationData":[OSD([sQuery(id+"F0.wireOp",EDGE,"E0"),sQuery(id+"F0.wireOp",EDGE,"E7.top"),sQuery(id+"F0.wireOp",EDGE,"E7.left"),sQuery(id+"F0.wireOp",EDGE,"E7.right"),sQuery(id+"F0.wireOp",EDGE,"E8"),sQuery(id+"F0.wireOp",EDGE,"E9"),sQuery(id+"F0.wireOp",EDGE,"E10"),sQuery(id+"F0.wireOp",EDGE,"E11")])],"isStart":false});
            var Q6;
            {var subQ0=sQuery(id+"F0.wireOp",EDGE,"E10");Q6=makeQuery(id+"F9.boolean.opBoolean","INTERSECT",EDGE,{"derivedFrom":[makeQuery(id+"F7.boolean.opBoolean","MERGE",FACE,{"derivedFrom":[makeQuery(id+"F1.opExtrude","SWEPT_FACE",FACE,{"disambiguationData":[OSD([subQ0])]}),makeQuery(id+"F7.opExtrude","SWEPT_FACE",FACE,{"disambiguationData":[OSD([subQ0])]})]}),makeQuery(id+"F9.opExtrude","SWEPT_FACE",FACE,{"disambiguationData":[OSD([sQuery(id+"F8.wireOp",EDGE,"E29")])]})]});}
            var Q7;
            {var subQ0=sQuery(id+"F0.wireOp",EDGE,"oxaJkNi3-Ak0Z-1hdz-Ji0s-hlfaC5dMFClf");var subQ1=sQuery(id+"F0.wireOp",EDGE,"E9");var subQ2=sQuery(id+"F0.wireOp",EDGE,"E7.left");var subQ3=sQuery(id+"F0.wireOp",EDGE,"E7.top");var subQ4=sQuery(id+"F0.wireOp",EDGE,"E10");var subQ5=sQuery(id+"F0.wireOp",EDGE,"E7.right");Q7=makeQuery(id+"F7.boolean.opBoolean","SPLIT",FACE,{"disambiguationData":[TD([makeQuery(id+"F1.opExtrude","SWEPT_FACE",FACE,{"disambiguationData":[OSD([subQ3])]})])],"derivedFrom":makeQuery(id+"F1.opExtrude","CAP_FACE",FACE,{"disambiguationData":[OSD([sQuery(id+"F0.wireOp",EDGE,"E0"),sQuery(id+"F0.wireOp",EDGE,"E1.top"),sQuery(id+"F0.wireOp",EDGE,"E1.left"),sQuery(id+"F0.wireOp",EDGE,"E1.right"),sQuery(id+"F0.wireOp",EDGE,"E2.MirrorCS"),sQuery(id+"F0.wireOp",EDGE,"E3.MirrorCS"),sQuery(id+"F0.wireOp",EDGE,"E4.MirrorCS"),sQuery(id+"F0.wireOp",EDGE,"E5.trimOffspring"),sQuery(id+"F0.wireOp",EDGE,"E6.trimOffspring"),subQ3,subQ2,subQ5,sQuery(id+"F0.wireOp",EDGE,"E8"),subQ1,subQ4,sQuery(id+"F0.wireOp",EDGE,"E11"),subQ0])],"isStart":true})});}
            var Q8;
            {var subQ0=sQuery(id+"F0.wireOp",EDGE,"E9");Q8=makeQuery(id+"F9.boolean.opBoolean","INTERSECT",EDGE,{"derivedFrom":[makeQuery(id+"F7.boolean.opBoolean","MERGE",FACE,{"derivedFrom":[makeQuery(id+"F1.opExtrude","SWEPT_FACE",FACE,{"disambiguationData":[OSD([subQ0])]}),makeQuery(id+"F7.opExtrude","SWEPT_FACE",FACE,{"disambiguationData":[OSD([subQ0])]})]}),makeQuery(id+"F9.opExtrude","SWEPT_FACE",FACE,{"disambiguationData":[OSD([sQuery(id+"F8.wireOp",EDGE,"E29")])]})]});}
            var Q9;
            {var subQ0=sQuery(id+"F0.wireOp",EDGE,"E7.top");Q9=makeQuery(id+"F7.boolean.opBoolean","MERGE",FACE,{"derivedFrom":[makeQuery(id+"F1.opExtrude","SWEPT_FACE",FACE,{"disambiguationData":[OSD([subQ0])]}),makeQuery(id+"F7.opExtrude","SWEPT_FACE",FACE,{"disambiguationData":[OSD([subQ0]),TDD([makeQuery(id+"F0.imprint","IMPRINT",EDGE,{"disambiguationData":[TD([[makeQuery(id+"F0.imprint","INTERSECT",VERTEX,{"derivedFrom":[subQ0,sQuery(id+"F0.wireOp",EDGE,"E7.left")]}),-1.0]])],"derivedFrom":subQ0})])]}),makeQuery(id+"F7.opExtrude","SWEPT_FACE",FACE,{"disambiguationData":[OSD([subQ0]),TDD([makeQuery(id+"F0.imprint","IMPRINT",EDGE,{"disambiguationData":[TD([[makeQuery(id+"F0.imprint","INTERSECT",VERTEX,{"derivedFrom":[subQ0,sQuery(id+"F0.wireOp",EDGE,"E7.right")]}),1.0]])],"derivedFrom":subQ0})])]})]});}
            var Q10;
            {var subQ0=sQuery(id+"F0.wireOp",EDGE,"E7.left");Q10=makeQuery(id+"F7.boolean.opBoolean","MERGE",FACE,{"derivedFrom":[makeQuery(id+"F1.opExtrude","SWEPT_FACE",FACE,{"disambiguationData":[OSD([subQ0])]}),makeQuery(id+"F7.opExtrude","SWEPT_FACE",FACE,{"disambiguationData":[OSD([subQ0])]})]});}
            var Q11;
            Q11=makeQuery(id+"F1.opExtrude","SWEPT_FACE",FACE,{"disambiguationData":[OSD([sQuery(id+"F0.wireOp",EDGE,"E2.MirrorCS")])]});
            var Q12;
            Q12=makeQuery(id+"F1.opExtrude","SWEPT_FACE",FACE,{"disambiguationData":[OSD([sQuery(id+"F0.wireOp",EDGE,"E1.left")])]});
            var Q13;
            Q13=makeQuery(id+"F1.opExtrude","SWEPT_FACE",FACE,{"disambiguationData":[OSD([sQuery(id+"F0.wireOp",EDGE,"E4.MirrorCS")])]});
            var Q14;
            {var subQ0=sQuery(id+"F0.wireOp",EDGE,"E12.trimOffspring");Q14=makeQuery(id+"F7.boolean.opBoolean","MERGE",FACE,{"derivedFrom":[makeQuery(id+"F1.opExtrude","SWEPT_FACE",FACE,{"disambiguationData":[OSD([subQ0])]}),makeQuery(id+"F7.opExtrude","SWEPT_FACE",FACE,{"disambiguationData":[OSD([subQ0])]})]});}
            var Q15;
            {var subQ0=sQuery(id+"F0.wireOp",EDGE,"E1.top");Q15=makeQuery(id+"F21.opChamfer","BLEND_FACE",FACE,{"disambiguationData":[OSD([subQ0]),TDD([makeQuery(id+"F1.opExtrude","CAP_EDGE",EDGE,{"disambiguationData":[OSD([subQ0])],"isStart":true})])]});}
            var Q16;
            {var subQ0=sQuery(id+"F0.wireOp",EDGE,"E3.MirrorCS");Q16=makeQuery(id+"F21.opChamfer","BLEND_FACE",FACE,{"disambiguationData":[OSD([subQ0]),TDD([makeQuery(id+"F1.opExtrude","CAP_EDGE",EDGE,{"disambiguationData":[OSD([subQ0])],"isStart":true})])]});}
            var Q17;
            {var subQ0=sQuery(id+"F0.wireOp",EDGE,"E1.top");Q17=makeQuery(id+"F21.opChamfer","BLEND_FACE",FACE,{"disambiguationData":[OSD([subQ0]),TDD([makeQuery(id+"F1.opExtrude","CAP_EDGE",EDGE,{"disambiguationData":[OSD([subQ0])],"isStart":false})])]});}
            var Q18;
            {var subQ0=sQuery(id+"F0.wireOp",EDGE,"E3.MirrorCS");Q18=makeQuery(id+"F21.opChamfer","BLEND_FACE",FACE,{"disambiguationData":[OSD([subQ0]),TDD([makeQuery(id+"F1.opExtrude","CAP_EDGE",EDGE,{"disambiguationData":[OSD([subQ0])],"isStart":false})])]});}
            chamfer(context, id + "F22", {"entities" : qUnion([Q0, Q1, Q2, Q3, Q4, Q5, Q6, Q7, Q8, Q9, Q10, Q11, Q12, Q13, Q14, Q15, Q16, Q17, Q18]), "width" : 1 * mm, "tangentPropagation" : true});
        }
    });
